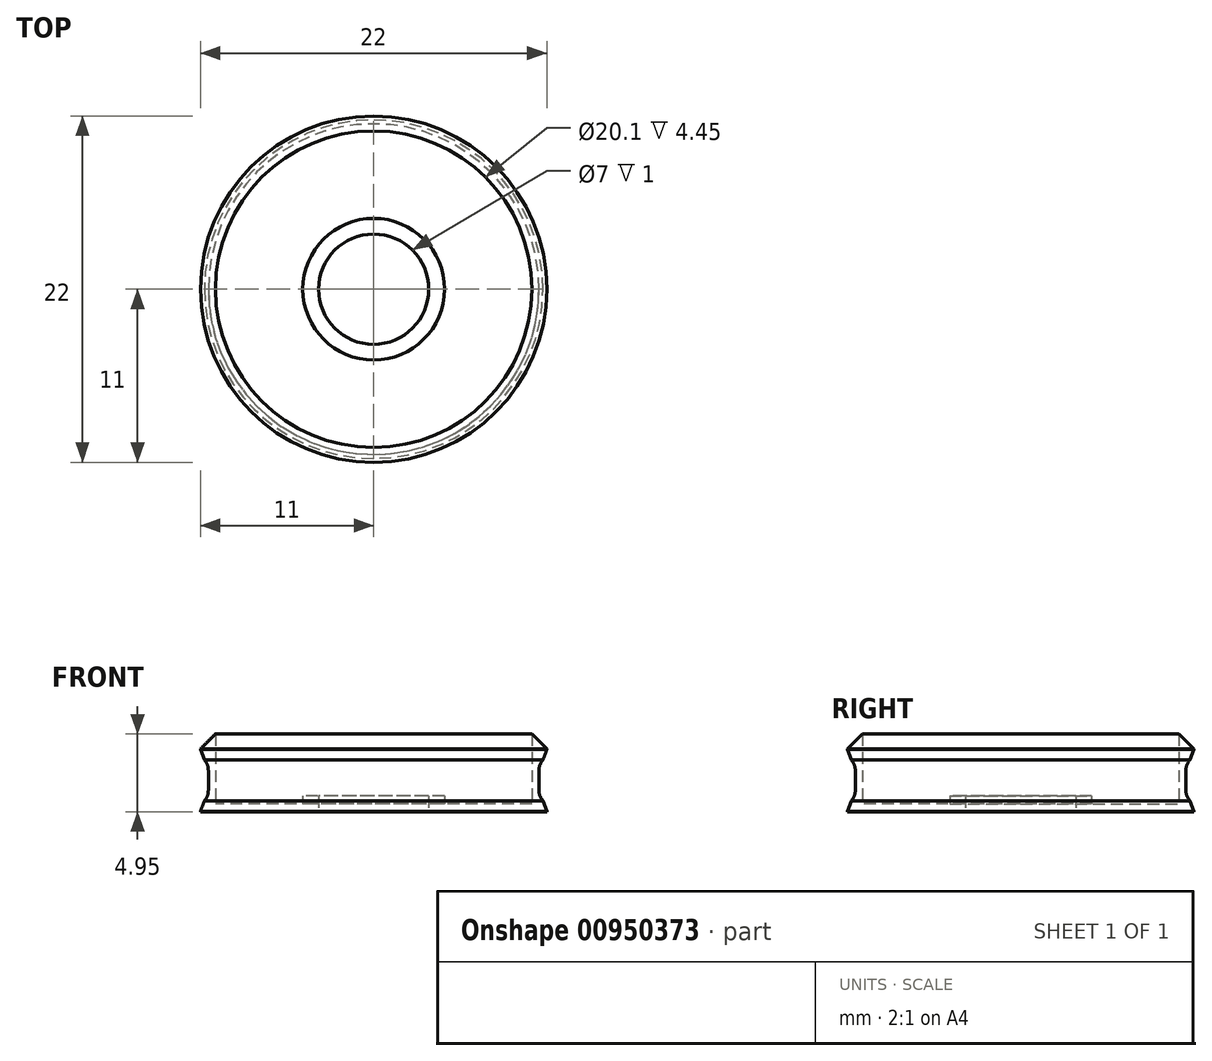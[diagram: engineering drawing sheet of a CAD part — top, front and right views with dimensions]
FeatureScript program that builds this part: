
annotation { "Feature Type Name" : "Feature", "Feature Type Description" : "" }
export const myFeature = defineFeature(function(context is Context, id is Id, definition is map)
    precondition{}
    {
        {
            var Q0;
            Q0=qCreatedBy(makeId("Top.planeOp"),FACE);
            var sketch = newSketch(context, id + "F0", { "sketchPlane" : qUnion([Q0])});
            skCircle(sketch, "E0", {"center": v(0, 0) * mm, "radius": 10.05 * mm});
            skCircle(sketch, "E1", {"center": v(0, 0) * mm, "radius": 11 * mm});
            skCircle(sketch, "E2", {"center": v(0, 0) * mm, "radius": 10.5 * mm});
            skCircle(sketch, "E3", {"center": v(0, 0) * mm, "radius": 3.5 * mm});
            skCircle(sketch, "E4", {"center": v(0, 0) * mm, "radius": 4.5 * mm});
            skSolve(sketch);
        }
        {
            var Q0;
            Q0 = qSketchRegion(id + "F0", true);
            var Q1;
            Q1=makeQuery(id+"F0.imprint","IMPRINT",FACE,{"disambiguationData":[TD([[makeQuery(id+"F0.imprint","IMPRINT",EDGE,{"derivedFrom":sQuery(id+"F0.wireOp",EDGE,"E0")}),-1.0]])]});
            extrude(context, id + "F1", {"entities" : qUnion([Q0, Q1]), "depth" : 5 * mm, "offsetDistance" : 25 * mm});
        }
        {
            var Q0;
            Q0=qCreatedBy(makeId("Front.planeOp"),FACE);
            var sketch = newSketch(context, id + "F2", { "sketchPlane" : qUnion([Q0])});
            skLineSegment(sketch, "E5", {"start": v(0, 0) * mm, "end": v(0, 5) * mm});
            skLineSegment(sketch, "E6", {"start": v(0, 0) * mm, "end": v(0, 2.5) * mm});
            skSolve(sketch);
        }
        {
            var Q0;
            Q0=sQuery(id+"F2.wireOp",VERTEX,"E6.end");
            var Q1;
            Q1=qCreatedBy(makeId("Top.planeOp"),FACE);
            cPlane(context, id + "F3", {"entities" : qUnion([Q0, Q1]), "cplaneType" : CPlaneType.PLANE_POINT, "offset" : 25 * mm, "width" : 150 * mm, "height" : 150 * mm});
        }
        {
            var Q0;
            Q0=qCreatedBy(id+"F3.planeOp",FACE);
            var sketch = newSketch(context, id + "F4", { "sketchPlane" : qUnion([Q0])});
            skCircle(sketch, "E7", {"center": v(0, 0) * mm, "radius": 10.5 * mm});
            skCircle(sketch, "E8", {"center": v(0, 0) * mm, "radius": 11 * mm});
            skSolve(sketch);
        }
        {
            var Q0;
            Q0 = qSketchRegion(id + "F4", true);
            extrude(context, id + "F5", {"entities" : qUnion([Q0]), "operationType" : NewBodyOperationType.REMOVE, "oppositeDirection" : true, "depth" : 2 * mm, "offsetDistance" : 25 * mm, "hasSecondDirection" : true, "secondDirectionOppositeDirection" : false, "secondDirectionDepth" : 1 * mm});
        }
        {
            var Q0;
            Q0=makeQuery(id+"F1.opExtrude","CAP_EDGE",EDGE,{"disambiguationData":[OSD([sQuery(id+"F0.wireOp",EDGE,"E1")])],"isStart":false});
            chamfer(context, id + "F6", {"entities" : qUnion([Q0]), "width" : 1 * mm, "tangentPropagation" : true});
        }
        {
            var Q0;
            Q0=makeQuery(id+"F5.boolean.opBoolean","COPY",EDGE,{"derivedFrom":makeQuery(id+"F5.opExtrude","CAP_EDGE",EDGE,{"disambiguationData":[OSD([sQuery(id+"F4.wireOp",EDGE,"E7")])],"isStart":true})});
            var Q1;
            Q1=makeQuery(id+"F5.boolean.opBoolean","COPY",EDGE,{"derivedFrom":makeQuery(id+"F5.opExtrude","CAP_EDGE",EDGE,{"disambiguationData":[OSD([sQuery(id+"F4.wireOp",EDGE,"E7")])],"isStart":false})});
            fillet(context, id + "F7", {"entities" : qUnion([Q0, Q1]), "radius" : 1 * mm, "tangentPropagation" : true, "allowEdgeOverflow" : false});
        }
        {
            var Q0;
            {var subQ0=sQuery(id+"F0.wireOp",EDGE,"E1");var subQ1=sQuery(id+"F4.wireOp",EDGE,"E7");Q0=makeQuery(id+"F7.opFillet","BLEND_EDGE",EDGE,{"blendedFrom":[makeQuery(id+"F5.boolean.opBoolean","COPY",EDGE,{"derivedFrom":makeQuery(id+"F5.opExtrude","CAP_EDGE",EDGE,{"disambiguationData":[OSD([subQ1])],"isStart":true})}),makeQuery(id+"F5.boolean.opBoolean","SPLIT",FACE,{"disambiguationData":[TD([makeQuery(id+"F1.opExtrude","CAP_FACE",FACE,{"disambiguationData":[OSD([sQuery(id+"F0.wireOp",EDGE,"E0"),subQ0])],"isStart":false})])],"derivedFrom":makeQuery(id+"F1.opExtrude","SWEPT_FACE",FACE,{"disambiguationData":[OSD([subQ0])]})})],"blendedInto":[makeQuery(id+"F5.boolean.opBoolean","SPLIT",FACE,{"disambiguationData":[TD([makeQuery(id+"F1.opExtrude","CAP_FACE",FACE,{"disambiguationData":[OSD([sQuery(id+"F0.wireOp",EDGE,"E0"),subQ0])],"isStart":false})])],"derivedFrom":makeQuery(id+"F1.opExtrude","SWEPT_FACE",FACE,{"disambiguationData":[OSD([subQ0])]})})]});}
            var Q1;
            {var subQ0=sQuery(id+"F0.wireOp",EDGE,"E1");var subQ1=sQuery(id+"F4.wireOp",EDGE,"E7");Q1=makeQuery(id+"F7.opFillet","BLEND_EDGE",EDGE,{"blendedFrom":[makeQuery(id+"F5.boolean.opBoolean","COPY",EDGE,{"derivedFrom":makeQuery(id+"F5.opExtrude","CAP_EDGE",EDGE,{"disambiguationData":[OSD([subQ1])],"isStart":false})}),makeQuery(id+"F5.boolean.opBoolean","SPLIT",FACE,{"disambiguationData":[TD([makeQuery(id+"F1.opExtrude","CAP_FACE",FACE,{"disambiguationData":[OSD([sQuery(id+"F0.wireOp",EDGE,"E0"),subQ0])],"isStart":true})])],"derivedFrom":makeQuery(id+"F1.opExtrude","SWEPT_FACE",FACE,{"disambiguationData":[OSD([subQ0])]})})],"blendedInto":[makeQuery(id+"F5.boolean.opBoolean","SPLIT",FACE,{"disambiguationData":[TD([makeQuery(id+"F1.opExtrude","CAP_FACE",FACE,{"disambiguationData":[OSD([sQuery(id+"F0.wireOp",EDGE,"E0"),subQ0])],"isStart":true})])],"derivedFrom":makeQuery(id+"F1.opExtrude","SWEPT_FACE",FACE,{"disambiguationData":[OSD([subQ0])]})})]});}
            chamfer(context, id + "F8", {"entities" : qUnion([Q0, Q1]), "width" : 1 * mm, "tangentPropagation" : true});
        }
        {
            var Q0;
            Q0=makeQuery(id+"F0.imprint","IMPRINT",FACE,{"disambiguationData":[TD([[makeQuery(id+"F0.imprint","IMPRINT",EDGE,{"derivedFrom":sQuery(id+"F0.wireOp",EDGE,"E0")}),1.0]])]});
            extrude(context, id + "F9", {"entities" : qUnion([Q0]), "operationType" : NewBodyOperationType.ADD, "depth" : .5 * mm, "offsetDistance" : 25 * mm});
        }
        {
            var Q0;
            Q0=makeQuery(id+"F0.imprint","IMPRINT",FACE,{"disambiguationData":[TD([[makeQuery(id+"F0.imprint","IMPRINT",EDGE,{"derivedFrom":sQuery(id+"F0.wireOp",EDGE,"E3")}),-1.0]])]});
            extrude(context, id + "F10", {"entities" : qUnion([Q0]), "operationType" : NewBodyOperationType.ADD, "depth" : 1 * mm, "offsetDistance" : 25 * mm});
        }
    });
